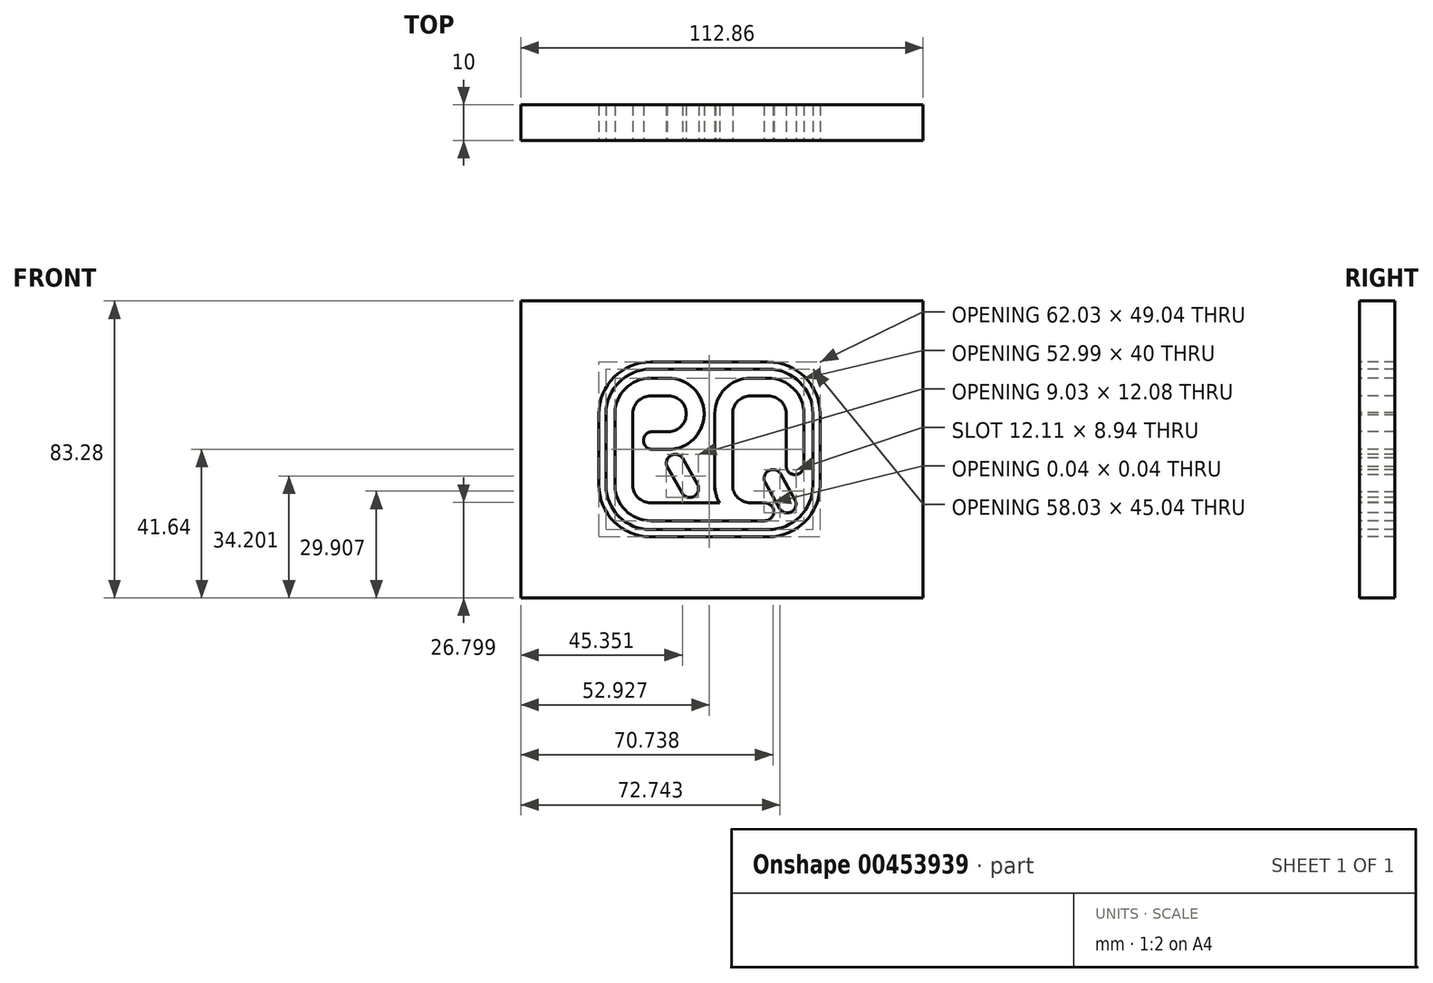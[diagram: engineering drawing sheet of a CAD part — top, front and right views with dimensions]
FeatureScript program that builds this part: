
annotation { "Feature Type Name" : "Feature", "Feature Type Description" : "" }
export const myFeature = defineFeature(function(context is Context, id is Id, definition is map)
    precondition{}
    {
        {
            var Q0;
            Q0=qCreatedBy(makeId("Front.planeOp"),FACE);
            var sketch = newSketch(context, id + "F0", { "sketchPlane" : qUnion([Q0])});
            skPoint(sketch, "E0.middle", {"position": v(0, 0) * mm});
            skLineSegment(sketch, "E1", {"start": v(-25, 10) * mm, "end": v(-25, -10) * mm});
            skLineSegment(sketch, "E2", {"start": v(-2, -20) * mm, "end": v(-0.38, -20) * mm});
            skLineSegment(sketch, "E3", {"start": v(-2, -11) * mm, "end": v(-2, 10) * mm});
            skLineSegment(sketch, "E4", {"start": v(8, 20) * mm, "end": v(13, 20) * mm});
            skLineSegment(sketch, "E5", {"start": v(23, 10) * mm, "end": v(23, -10) * mm});
            skLineSegment(sketch, "E6", {"start": v(13, -20) * mm, "end": v(9, -20) * mm});
            skLineSegment(sketch, "E7", {"start": v(-25, 20) * mm, "end": v(-15, 20) * mm});
            skLineSegment(sketch, "E8", {"start": v(-19.5, 0) * mm, "end": v(-15, 0) * mm});
            skLineSegment(sketch, "E9", {"start": v(-5, 10.33) * mm, "end": v(-5, 10.33) * mm});
            skPoint(sketch, "E10.visualSharp", {"position": v(-5.33, 20) * mm});
            skArc(sketch, "E10.filletArc", {"start": v(-5, 10.33) * mm, "mid": v(-8.05, 17.19) * mm, "end": v(-15, 20) * mm});
            skArc(sketch, "E11.filletArc", {"start": v(-15, 0) * mm, "mid": v(-7.81, 3.05) * mm, "end": v(-5, 10.33) * mm});
            skPoint(sketch, "E12.visualSharp", {"position": v(-3.63, -20) * mm});
            skPoint(sketch, "E13.visualSharp", {"position": v(23, -20) * mm});
            skPoint(sketch, "E14.visualSharp", {"position": v(23, 20) * mm});
            skArc(sketch, "E14.filletArc", {"start": v(23, 10) * mm, "mid": v(20.07, 17.07) * mm, "end": v(13, 20) * mm});
            skPoint(sketch, "E15.visualSharp", {"position": v(-2, 20) * mm});
            skArc(sketch, "E15.filletArc", {"start": v(8, 20) * mm, "mid": v(0.92, 17.07) * mm, "end": v(-2, 10) * mm});
            skPoint(sketch, "E16.visualSharp", {"position": v(-2, -20) * mm});
            skArc(sketch, "E17.0", {"start": v(8, 15) * mm, "mid": v(4.46, 13.54) * mm, "end": v(3, 10) * mm});
            skLineSegment(sketch, "E17.1", {"start": v(3, -11) * mm, "end": v(3, 10) * mm});
            skLineSegment(sketch, "E17.2", {"start": v(8, 15) * mm, "end": v(13, 15) * mm});
            skArc(sketch, "E17.4", {"start": v(18, 10) * mm, "mid": v(16.53, 13.54) * mm, "end": v(13, 15) * mm});
            skLineSegment(sketch, "E17.5", {"start": v(18, 10) * mm, "end": v(18, -10) * mm});
            skArc(sketch, "E17.6", {"start": v(14.29, -14.83) * mm, "mid": v(14.3, -14.82) * mm, "end": v(14.33, -14.82) * mm});
            skLineSegment(sketch, "E17.7", {"start": v(13, -15) * mm, "end": v(9, -15) * mm});
            skArc(sketch, "E18.1", {"start": v(-15, 5) * mm, "mid": v(-11.44, 6.5) * mm, "end": v(-10, 10.08) * mm});
            skArc(sketch, "E18.2", {"start": v(-10, 10.08) * mm, "mid": v(-11.5, 13.56) * mm, "end": v(-15, 15) * mm});
            skLineSegment(sketch, "E18.3", {"start": v(-20, 15) * mm, "end": v(-15, 15) * mm});
            skLineSegment(sketch, "E19.0", {"start": v(-30, 17.5) * mm, "end": v(-30, -10) * mm});
            skLineSegment(sketch, "E20.0", {"start": v(-1, -15) * mm, "end": v(-0.38, -15) * mm});
            skLineSegment(sketch, "E21", {"start": v(-20, -20) * mm, "end": v(-2, -20) * mm});
            skLineSegment(sketch, "E22", {"start": v(-1, -15) * mm, "end": v(0, -15) * mm});
            skLineSegment(sketch, "E23.0", {"start": v(-20, -15) * mm, "end": v(0, -15) * mm});
            skLineSegment(sketch, "E24", {"start": v(-5, 10.33) * mm, "end": v(-5, 0) * mm});
            skLineSegment(sketch, "E25", {"start": v(0.5, -13.5) * mm, "end": v(0.5, -13.5) * mm});
            skPoint(sketch, "E26.visualSharp", {"position": v(3, -13.5) * mm});
            skArc(sketch, "E26.filletArc", {"start": v(0.5, -13.5) * mm, "mid": v(2.26, -12.77) * mm, "end": v(3, -11) * mm, "construction": true});
            skPoint(sketch, "E27.newPointB", {"position": v(-23.5, -13.5) * mm});
            skArc(sketch, "E27.filletArc", {"start": v(-2, -11) * mm, "mid": v(-1.27, -12.77) * mm, "end": v(0.5, -13.5) * mm});
            skPoint(sketch, "E28.visualSharp", {"position": v(-30, -20) * mm});
            skArc(sketch, "E28.filletArc", {"start": v(-30, -19.5) * mm, "mid": v(-29.85, -19.85) * mm, "end": v(-29.5, -20) * mm});
            skLineSegment(sketch, "E29", {"start": v(-7.28, -12.77) * mm, "end": v(-7.28, -12.77) * mm});
            skArc(sketch, "E30.filletArc", {"start": v(-7.28, -12.77) * mm, "mid": v(-6.55, -11) * mm, "end": v(-7.27, -9.24) * mm});
            skArc(sketch, "E31.filletArc", {"start": v(-11.23, -12.21) * mm, "mid": v(-9.4, -13.48) * mm, "end": v(-7.28, -12.77) * mm});
            skLineSegment(sketch, "E32.0", {"start": v(14.32, -14.86) * mm, "end": v(14.29, -14.83) * mm});
            skPoint(sketch, "E33.newPointB", {"position": v(-25, 20) * mm});
            skPoint(sketch, "E34.visualSharp", {"position": v(-23.5, 5) * mm});
            skPoint(sketch, "E35.visualSharp", {"position": v(-23.5, 0) * mm});
            skLineSegment(sketch, "E36", {"start": v(-30, 10) * mm, "end": v(-30, 17.5) * mm});
            skLineSegment(sketch, "E37", {"start": v(-20, 20) * mm, "end": v(-25, 20) * mm});
            skPoint(sketch, "E38.visualSharp", {"position": v(-30, 20) * mm});
            skArc(sketch, "E38.filletArc", {"start": v(-20, 20) * mm, "mid": v(-27.07, 17.07) * mm, "end": v(-30, 10) * mm});
            skPoint(sketch, "E39", {"position": v(19.6, -17.6) * mm});
            skPoint(sketch, "E40.orphan", {"position": v(17, -13) * mm});
            skLineSegment(sketch, "E41.trimOffspring", {"start": v(13, -20) * mm, "end": v(-0.38, -20) * mm});
            skPoint(sketch, "E42.newPointB", {"position": v(-25, -20) * mm});
            skArc(sketch, "E42.filletArc", {"start": v(-25, -10) * mm, "mid": v(-23.54, -13.54) * mm, "end": v(-20, -15) * mm});
            skLineSegment(sketch, "E43", {"start": v(-15, 20) * mm, "end": v(8, 20) * mm});
            skLineSegment(sketch, "E44", {"start": v(21.86, -24.52) * mm, "end": v(-20, -24.52) * mm});
            skLineSegment(sketch, "E45", {"start": v(27.51, -22.02) * mm, "end": v(27.51, -18.86) * mm});
            skLineSegment(sketch, "E46", {"start": v(13, 24.52) * mm, "end": v(-20, 24.52) * mm});
            skLineSegment(sketch, "E47", {"start": v(-34.52, -10) * mm, "end": v(-34.52, 10) * mm});
            skPoint(sketch, "E48.orphan", {"position": v(17.43, -17.97) * mm});
            skPoint(sketch, "E49.orphan", {"position": v(13.35, -13.89) * mm});
            skArc(sketch, "E50.0", {"start": v(27.51, 10) * mm, "mid": v(23.26, 20.27) * mm, "end": v(13, 24.52) * mm});
            skArc(sketch, "E51.0", {"start": v(25.51, 10) * mm, "mid": v(21.85, 18.85) * mm, "end": v(13, 22.52) * mm});
            skLineSegment(sketch, "E52.0", {"start": v(25.51, -22.07) * mm, "end": v(25.51, -18.99) * mm});
            skLineSegment(sketch, "E53.0", {"start": v(25.02, -22.52) * mm, "end": v(21.98, -22.52) * mm});
            skLineSegment(sketch, "E54.0", {"start": v(-32.52, -10) * mm, "end": v(-32.52, 10) * mm});
            skLineSegment(sketch, "E55.0", {"start": v(13, 22.52) * mm, "end": v(-20, 22.52) * mm});
            skPoint(sketch, "E56.visualSharp", {"position": v(-32.52, 22.52) * mm});
            skArc(sketch, "E56.filletArc", {"start": v(-20, 22.52) * mm, "mid": v(-28.85, 18.85) * mm, "end": v(-32.52, 10) * mm});
            skArc(sketch, "E57.0", {"start": v(-20, 24.52) * mm, "mid": v(-30.27, 20.27) * mm, "end": v(-34.52, 10) * mm});
            skPoint(sketch, "E58.visualSharp", {"position": v(-32.52, -22.52) * mm});
            skLineSegment(sketch, "E59", {"start": v(26.51, -15) * mm, "end": v(26.51, -16.32) * mm});
            skLineSegment(sketch, "E60.0", {"start": v(18.1, -20.77) * mm, "end": v(22.19, -24.85) * mm, "construction": true});
            skLineSegment(sketch, "E61.0", {"start": v(23.76, -15.1) * mm, "end": v(27.84, -19.2) * mm, "construction": true});
            skLineSegment(sketch, "E62.trimOffspring", {"start": v(25.51, -14) * mm, "end": v(25.51, 10) * mm});
            skLineSegment(sketch, "E63.trimOffspring", {"start": v(27.51, -14) * mm, "end": v(27.51, 33) * mm});
            skLineSegment(sketch, "E64.trimOffspring", {"start": v(19.86, -22.52) * mm, "end": v(-20, -22.52) * mm});
            skLineSegment(sketch, "E65", {"start": v(21.86, -24.52) * mm, "end": v(25.02, -24.52) * mm});
            skLineSegment(sketch, "E66", {"start": v(27.51, -14) * mm, "end": v(27.51, -22.02) * mm});
            skLineSegment(sketch, "E67.bottom", {"start": v(-56.43, 41.64) * mm, "end": v(56.43, 41.64) * mm});
            skLineSegment(sketch, "E67.top", {"start": v(-56.43, -41.64) * mm, "end": v(56.43, -41.64) * mm});
            skLineSegment(sketch, "E67.left", {"start": v(-56.43, 41.64) * mm, "end": v(-56.43, -41.64) * mm});
            skLineSegment(sketch, "E67.right", {"start": v(56.43, 41.64) * mm, "end": v(56.43, -41.64) * mm});
            skLineSegment(sketch, "E68", {"start": v(0, 0) * mm, "end": v(0, -38.7) * mm, "construction": true});
            skLineSegment(sketch, "E69", {"start": v(0, 0) * mm, "end": v(33.56, 0) * mm, "construction": true});
            skArc(sketch, "E70.filletArc", {"start": v(-20, 15) * mm, "mid": v(-23.54, 13.54) * mm, "end": v(-25, 10) * mm});
            skArc(sketch, "E71.0", {"start": v(-30, -10) * mm, "mid": v(-27.07, -17.07) * mm, "end": v(-20, -20) * mm});
            skArc(sketch, "E72.0", {"start": v(-34.52, -10) * mm, "mid": v(-30.27, -20.27) * mm, "end": v(-20, -24.52) * mm});
            skArc(sketch, "E73.0", {"start": v(-32.52, -10) * mm, "mid": v(-28.85, -18.85) * mm, "end": v(-20, -22.52) * mm});
            skLineSegment(sketch, "E74", {"start": v(-15, 5) * mm, "end": v(-19.5, 5) * mm});
            skLineSegment(sketch, "E75", {"start": v(-23.5, 2.5) * mm, "end": v(-23.5, 2.5) * mm});
            skArc(sketch, "E76.filletArc", {"start": v(-21, 5) * mm, "mid": v(-22.77, 4.27) * mm, "end": v(-23.5, 2.5) * mm, "construction": true});
            skArc(sketch, "E77.filletArc", {"start": v(-23.5, 2.5) * mm, "mid": v(-22.77, 0.73) * mm, "end": v(-21, 0) * mm, "construction": true});
            skPoint(sketch, "E78.startSnap0", {"position": v(-6.55, -11) * mm});
            skLineSegment(sketch, "E79", {"start": v(-22.87, 0.84) * mm, "end": v(-10.92, -12.66) * mm, "construction": true});
            skLineSegment(sketch, "E80.0", {"start": v(-19.13, 4.16) * mm, "end": v(-7.17, -9.34) * mm, "construction": true});
            skArc(sketch, "E81.0", {"start": v(13, -22.52) * mm, "mid": v(21.85, -18.85) * mm, "end": v(25.51, -10) * mm});
            skArc(sketch, "E82.0", {"start": v(13, -24.52) * mm, "mid": v(23.26, -20.27) * mm, "end": v(27.51, -10) * mm});
            skCircle(sketch, "E83", {"center": v(18.3, -15.3) * mm, "radius": 2.5 * mm});
            skLineSegment(sketch, "E84", {"start": v(-21, 5) * mm, "end": v(-21, 0) * mm, "construction": true});
            skLineSegment(sketch, "E85", {"start": v(-21, 5) * mm, "end": v(-18.16, 0) * mm});
            skLineSegment(sketch, "E86.0", {"start": v(-16.65, 7.47) * mm, "end": v(-12.58, 0.3) * mm});
            skLineSegment(sketch, "E87", {"start": v(-22, 7.3) * mm, "end": v(-22, -4.59) * mm});
            skLineSegment(sketch, "E88", {"start": v(-28.56, 2.5) * mm, "end": v(-6.16, 2.5) * mm, "construction": true});
            skCircle(sketch, "E89", {"center": v(-19.5, 2.5) * mm, "radius": 2.5 * mm});
            skArc(sketch, "E90.0", {"start": v(14.33, -14.82) * mm, "mid": v(14.32, -14.84) * mm, "end": v(14.32, -14.86) * mm});
            skLineSegment(sketch, "E91", {"start": v(10.5, 15) * mm, "end": v(10.5, 5.39) * mm, "construction": true});
            skArc(sketch, "E92.MirrorCS", {"start": v(8, -15) * mm, "mid": v(4.46, -13.54) * mm, "end": v(3, -10) * mm});
            skArc(sketch, "E93.MirrorCS", {"start": v(8, -20) * mm, "mid": v(0.92, -17.07) * mm, "end": v(-2, -10) * mm});
            skLineSegment(sketch, "E94.trimOffspring", {"start": v(8, -15) * mm, "end": v(9, -15) * mm});
            skArc(sketch, "E95", {"start": v(12.04, -20) * mm, "mid": v(14.54, -17.5) * mm, "end": v(12.04, -15) * mm});
            skArc(sketch, "E96", {"start": v(18, -4.59) * mm, "mid": v(20.5, -7.09) * mm, "end": v(23, -4.59) * mm});
            skCircle(sketch, "E97", {"center": v(14.33, -8.16) * mm, "radius": 2.5 * mm});
            skLineSegment(sketch, "E98", {"start": v(-11.07, -2.36) * mm, "end": v(-15.42, -4.83) * mm});
            skArc(sketch, "E99", {"start": v(-10.92, -2.63) * mm, "mid": v(-14.33, -1.7) * mm, "end": v(-15.27, -5.1) * mm});
            skLineSegment(sketch, "E100.trimOffspring", {"start": v(-11.07, -2.36) * mm, "end": v(-6.74, -10) * mm});
            skLineSegment(sketch, "E101.trimOffspring", {"start": v(-15.42, -4.83) * mm, "end": v(-11.1, -12.46) * mm});
            skLineSegment(sketch, "E102", {"start": v(19.55, -17.47) * mm, "end": v(13.03, -6) * mm, "construction": true});
            skLineSegment(sketch, "E103", {"start": v(16.51, -6.95) * mm, "end": v(20.48, -14.09) * mm});
            skLineSegment(sketch, "E104", {"start": v(12.14, -9.38) * mm, "end": v(16.11, -16.52) * mm});
            skSolve(sketch);
        }
        {
            var Q0;
            Q0=makeQuery(id+"F0.imprint","IMPRINT",FACE,{"disambiguationData":[TD([[makeQuery(id+"F0.imprint","IMPRINT",EDGE,{"derivedFrom":sQuery(id+"F0.wireOp",EDGE,"E1")}),-1.0]])]});
            var Q1;
            {var subQ6=sQuery(id+"F0.wireOp",EDGE,"8dgEX87s-OnN3-UPAw-RyUf-tcfM0RuKeMZf");Q1=makeQuery(id+"F0.imprint","IMPRINT",FACE,{"disambiguationData":[TD([[makeQuery(id+"F0.imprint","IMPRINT",EDGE,{"derivedFrom":subQ6}),1.0]])]});}
            var Q2;
            {var subQ0=sQuery(id+"F0.wireOp",EDGE,"S70SFG3v-wlmV-iE8w-7gkR-MiBzXbBwRlH9");var subQ1=makeQuery(id+"F0.imprint","INTERSECT",VERTEX,{"derivedFrom":[sQuery(id+"F0.wireOp",EDGE,"c0c087a9-fd36-4214-a694-875f0f01d769.0"),subQ0]});Q2=makeQuery(id+"F0.imprint","IMPRINT",FACE,{"disambiguationData":[TD([[makeQuery(id+"F0.imprint","IMPRINT",EDGE,{"disambiguationData":[TD([[subQ1,-1.0]])],"derivedFrom":subQ0}),1.0]])]});}
            var Q3;
            {var subQ1=sQuery(id+"F0.wireOp",EDGE,"c0c087a9-fd36-4214-a694-875f0f01d769.0");Q3=makeQuery(id+"F0.imprint","IMPRINT",FACE,{"disambiguationData":[TD([[makeQuery(id+"F0.imprint","IMPRINT",EDGE,{"derivedFrom":subQ1}),-1.0]])]});}
            var Q4;
            {var subQ0=sQuery(id+"F0.wireOp",EDGE,"E0.bottom");Q4=makeQuery(id+"F0.imprint","IMPRINT",FACE,{"disambiguationData":[TD([[makeQuery(id+"F0.imprint","IMPRINT",EDGE,{"derivedFrom":subQ0}),-1.0]])]});}
            var Q5;
            {var subQ0=sQuery(id+"F0.wireOp",EDGE,"E0.bottom");Q5=makeQuery(id+"F0.imprint","IMPRINT",FACE,{"disambiguationData":[TD([[makeQuery(id+"F0.imprint","IMPRINT",EDGE,{"derivedFrom":subQ0}),1.0]])]});}
            var Q6;
            {var subQ3=sQuery(id+"F0.wireOp",EDGE,"E8");var subQ7=sQuery(id+"F0.wireOp",EDGE,"E11.filletArc");var subQ8=makeQuery(id+"F0.imprint","INTERSECT",VERTEX,{"derivedFrom":[subQ3,subQ7]});Q6=makeQuery(id+"F0.imprint","IMPRINT",FACE,{"disambiguationData":[TD([[makeQuery(id+"F0.imprint","IMPRINT",EDGE,{"disambiguationData":[TD([[subQ8,1.0]])],"derivedFrom":subQ3}),1.0]])]});}
            var Q7;
            {var subQ4=sQuery(id+"F0.wireOp",EDGE,"E76.filletArc");Q7=makeQuery(id+"F0.imprint","IMPRINT",FACE,{"disambiguationData":[TD([[makeQuery(id+"F0.imprint","IMPRINT",EDGE,{"derivedFrom":subQ4}),1.0]])]});}
            var Q8;
            {var subQ0=sQuery(id+"F0.wireOp",EDGE,"E31.filletArc");Q8=makeQuery(id+"F0.imprint","IMPRINT",FACE,{"disambiguationData":[TD([[makeQuery(id+"F0.imprint","IMPRINT",EDGE,{"derivedFrom":subQ0}),1.0]])]});}
            var Q9;
            Q9=makeQuery(id+"F0.imprint","IMPRINT",FACE,{"disambiguationData":[TD([[makeQuery(id+"F0.imprint","IMPRINT",EDGE,{"derivedFrom":sQuery(id+"F0.wireOp",EDGE,"E83")}),1.0]])]});
            var Q10;
            {var subQ0=sQuery(id+"F0.wireOp",EDGE,"E88");var subQ1=sQuery(id+"F0.wireOp",EDGE,"E11.filletArc");var subQ2=makeQuery(id+"F0.imprint","INTERSECT",VERTEX,{"derivedFrom":[subQ1,subQ0]});Q10=makeQuery(id+"F0.imprint","IMPRINT",FACE,{"disambiguationData":[TD([[makeQuery(id+"F0.imprint","IMPRINT",EDGE,{"disambiguationData":[TD([[subQ2,1.0]])],"derivedFrom":subQ1}),1.0]])]});}
            var Q11;
            {var subQ0=sQuery(id+"F0.wireOp",EDGE,"E89");var subQ1=sQuery(id+"F0.wireOp",EDGE,"E74");var subQ2=makeQuery(id+"F0.imprint","INTERSECT",VERTEX,{"derivedFrom":[subQ1,subQ0]});Q11=makeQuery(id+"F0.imprint","IMPRINT",FACE,{"disambiguationData":[TD([[makeQuery(id+"F0.imprint","IMPRINT",EDGE,{"disambiguationData":[TD([[subQ2,1.0]])],"derivedFrom":subQ1}),1.0]])]});}
            var Q12;
            {var subQ0=sQuery(id+"F0.wireOp",EDGE,"E88");var subQ1=sQuery(id+"F0.wireOp",EDGE,"E85");var subQ2=makeQuery(id+"F0.imprint","INTERSECT",VERTEX,{"derivedFrom":[subQ1,subQ0]});Q12=makeQuery(id+"F0.imprint","IMPRINT",FACE,{"disambiguationData":[TD([[makeQuery(id+"F0.imprint","IMPRINT",EDGE,{"disambiguationData":[TD([[subQ2,-1.0]])],"derivedFrom":subQ1}),-1.0]])]});}
            var Q13;
            {var subQ0=sQuery(id+"F0.wireOp",EDGE,"E89");var subQ1=sQuery(id+"F0.wireOp",EDGE,"E85");var subQ2=makeQuery(id+"F0.imprint","INTERSECT",VERTEX,{"disambiguationData":[OD(0.0)],"derivedFrom":[subQ1,subQ0]});Q13=makeQuery(id+"F0.imprint","IMPRINT",FACE,{"disambiguationData":[TD([[makeQuery(id+"F0.imprint","IMPRINT",EDGE,{"disambiguationData":[TD([[subQ2,-1.0]])],"derivedFrom":subQ1}),-1.0]])]});}
            var Q14;
            {var subQ0=sQuery(id+"F0.wireOp",EDGE,"E89");var subQ1=sQuery(id+"F0.wireOp",EDGE,"E85");var subQ2=makeQuery(id+"F0.imprint","INTERSECT",VERTEX,{"disambiguationData":[OD(0.0)],"derivedFrom":[subQ1,subQ0]});Q14=makeQuery(id+"F0.imprint","IMPRINT",FACE,{"disambiguationData":[TD([[makeQuery(id+"F0.imprint","IMPRINT",EDGE,{"disambiguationData":[TD([[subQ2,-1.0]])],"derivedFrom":subQ1}),1.0]])]});}
            var Q15;
            {var subQ0=sQuery(id+"F0.wireOp",EDGE,"E88");var subQ1=sQuery(id+"F0.wireOp",EDGE,"E85");var subQ2=makeQuery(id+"F0.imprint","INTERSECT",VERTEX,{"derivedFrom":[subQ1,subQ0]});Q15=makeQuery(id+"F0.imprint","IMPRINT",FACE,{"disambiguationData":[TD([[makeQuery(id+"F0.imprint","IMPRINT",EDGE,{"disambiguationData":[TD([[subQ2,-1.0]])],"derivedFrom":subQ1}),1.0]])]});}
            var Q16;
            {var subQ0=sQuery(id+"F0.wireOp",EDGE,"E89");var subQ1=sQuery(id+"F0.wireOp",EDGE,"E8");var subQ2=makeQuery(id+"F0.imprint","INTERSECT",VERTEX,{"derivedFrom":[subQ1,subQ0]});Q16=makeQuery(id+"F0.imprint","IMPRINT",FACE,{"disambiguationData":[TD([[makeQuery(id+"F0.imprint","IMPRINT",EDGE,{"disambiguationData":[TD([[subQ2,-1.0]])],"derivedFrom":subQ1}),1.0]])]});}
            var Q17;
            Q17=makeQuery(id+"F0.imprint","IMPRINT",FACE,{"disambiguationData":[TD([[makeQuery(id+"F0.imprint","IMPRINT",EDGE,{"derivedFrom":sQuery(id+"F0.wireOp",EDGE,"E4")}),-1.0]])]});
            var Q18;
            {var subQ0=sQuery(id+"F0.wireOp",EDGE,"E97");var subQ1=sQuery(id+"F0.wireOp",EDGE,"l3Agq5ap-yWmA-VVue-g4vt-Hq9HFho2LNEB");var subQ2=makeQuery(id+"F0.imprint","INTERSECT",VERTEX,{"disambiguationData":[OD(0.0)],"derivedFrom":[subQ1,subQ0]});Q18=makeQuery(id+"F0.imprint","IMPRINT",FACE,{"disambiguationData":[TD([[makeQuery(id+"F0.imprint","IMPRINT",EDGE,{"disambiguationData":[TD([[subQ2,1.0]])],"derivedFrom":subQ1}),-1.0]])]});}
            var Q19;
            {var subQ0=sQuery(id+"F0.wireOp",EDGE,"E97");var subQ1=sQuery(id+"F0.wireOp",EDGE,"l3Agq5ap-yWmA-VVue-g4vt-Hq9HFho2LNEB");var subQ2=makeQuery(id+"F0.imprint","INTERSECT",VERTEX,{"disambiguationData":[OD(0.0)],"derivedFrom":[subQ1,subQ0]});Q19=makeQuery(id+"F0.imprint","IMPRINT",FACE,{"disambiguationData":[TD([[makeQuery(id+"F0.imprint","IMPRINT",EDGE,{"disambiguationData":[TD([[subQ2,1.0]])],"derivedFrom":subQ1}),1.0]])]});}
            var Q20;
            {var subQ0=sQuery(id+"F0.wireOp",EDGE,"m8UYtWHv-qO4X-QN6X-iKXV-4yPTMy5MIqK1");Q20=makeQuery(id+"F0.imprint","IMPRINT",FACE,{"disambiguationData":[TD([[makeQuery(id+"F0.imprint","IMPRINT",EDGE,{"derivedFrom":subQ0}),-1.0]])]});}
            var Q21;
            {var subQ4=sQuery(id+"F0.wireOp",EDGE,"GEM00Yna-KXC5-UJpv-niI3-6qlbkwYTooAT");Q21=makeQuery(id+"F0.imprint","IMPRINT",FACE,{"disambiguationData":[TD([[makeQuery(id+"F0.imprint","IMPRINT",EDGE,{"derivedFrom":subQ4}),1.0]])]});}
            var Q22;
            {var subQ0=sQuery(id+"F0.wireOp",EDGE,"E99");var subQ1=sQuery(id+"F0.wireOp",EDGE,"E98");var subQ2=makeQuery(id+"F0.imprint","INTERSECT",VERTEX,{"disambiguationData":[OD(0.0)],"derivedFrom":[subQ1,subQ0]});Q22=makeQuery(id+"F0.imprint","IMPRINT",FACE,{"disambiguationData":[TD([[makeQuery(id+"F0.imprint","IMPRINT",EDGE,{"disambiguationData":[TD([[subQ2,-1.0]])],"derivedFrom":subQ1}),-1.0]])]});}
            var Q23;
            {var subQ6=sQuery(id+"F0.wireOp",EDGE,"E104");Q23=makeQuery(id+"F0.imprint","IMPRINT",FACE,{"disambiguationData":[TD([[makeQuery(id+"F0.imprint","IMPRINT",EDGE,{"derivedFrom":subQ6}),1.0]])]});}
            var Q24;
            {var subQ0=sQuery(id+"F0.wireOp",EDGE,"E97");var subQ1=makeQuery(id+"F0.imprint","INTERSECT",VERTEX,{"derivedFrom":[subQ0,sQuery(id+"F0.wireOp",EDGE,"E103")]});Q24=makeQuery(id+"F0.imprint","IMPRINT",FACE,{"disambiguationData":[TD([[makeQuery(id+"F0.imprint","IMPRINT",EDGE,{"disambiguationData":[TD([[subQ1,-1.0]])],"derivedFrom":subQ0}),1.0]])]});}
            extrude(context, id + "F1", {"entities" : qUnion([Q0, Q1, Q2, Q3, Q4, Q5, Q6, Q7, Q8, Q9, Q10, Q11, Q12, Q13, Q14, Q15, Q16, Q17, Q18, Q19, Q20, Q21, Q22, Q23, Q24]), "oppositeDirection" : true, "depth" : 10 * mm});
        }
        {
            var Q0;
            Q0=makeQuery(id+"F0.imprint","IMPRINT",FACE,{"disambiguationData":[TD([[makeQuery(id+"F0.imprint","IMPRINT",EDGE,{"derivedFrom":sQuery(id+"F0.wireOp",EDGE,"E1")}),1.0]])]});
            var Q1;
            {var subQ16=sQuery(id+"F0.wireOp",EDGE,"E2");Q1=makeQuery(id+"F0.imprint","IMPRINT",FACE,{"disambiguationData":[TD([[makeQuery(id+"F0.imprint","IMPRINT",EDGE,{"derivedFrom":subQ16}),-1.0]])]});}
            extrude(context, id + "F2", {"entities" : qUnion([Q0, Q1]), "oppositeDirection" : true, "depth" : 10 * mm});
        }
        {
            var Q0;
            Q0=makeQuery(id+"F0.imprint","IMPRINT",FACE,{"disambiguationData":[TD([[makeQuery(id+"F0.imprint","IMPRINT",EDGE,{"derivedFrom":sQuery(id+"F0.wireOp",EDGE,"E46")}),1.0]])]});
            var Q1;
            {var subQ0=sQuery(id+"F0.wireOp",EDGE,"aTrX08yB-o83u-csdW-HvKf-6qn933KxLSEO");var subQ2=makeQuery(id+"F0.imprint","IMPRINT",VERTEX,{"derivedFrom":subQ0});Q1=makeQuery(id+"F0.imprint","IMPRINT",FACE,{"disambiguationData":[TD([[makeQuery(id+"F0.imprint","IMPRINT",EDGE,{"disambiguationData":[TD([[subQ2,-1.0]])],"derivedFrom":subQ0}),1.0]])]});}
            var Q2;
            {var subQ0=sQuery(id+"F0.wireOp",EDGE,"orb3SBHr-i0Mj-h6B2-otKM-5Ab6eh35dINg");var subQ3=makeQuery(id+"F0.imprint","IMPRINT",VERTEX,{"derivedFrom":subQ0});Q2=makeQuery(id+"F0.imprint","IMPRINT",FACE,{"disambiguationData":[TD([[makeQuery(id+"F0.imprint","IMPRINT",EDGE,{"disambiguationData":[TD([[subQ3,1.0]])],"derivedFrom":subQ0}),1.0]])]});}
            extrude(context, id + "F3", {"entities" : qUnion([Q0, Q1, Q2]), "oppositeDirection" : true, "depth" : 10 * mm});
        }
        {
            var Q0;
            Q0=makeQuery(id+"F0.imprint","IMPRINT",FACE,{"disambiguationData":[TD([[makeQuery(id+"F0.imprint","IMPRINT",EDGE,{"derivedFrom":sQuery(id+"F0.wireOp",EDGE,"E46")}),-1.0]])]});
            extrude(context, id + "F4", {"entities" : qUnion([Q0]), "oppositeDirection" : true, "depth" : 10 * mm});
        }
    });
